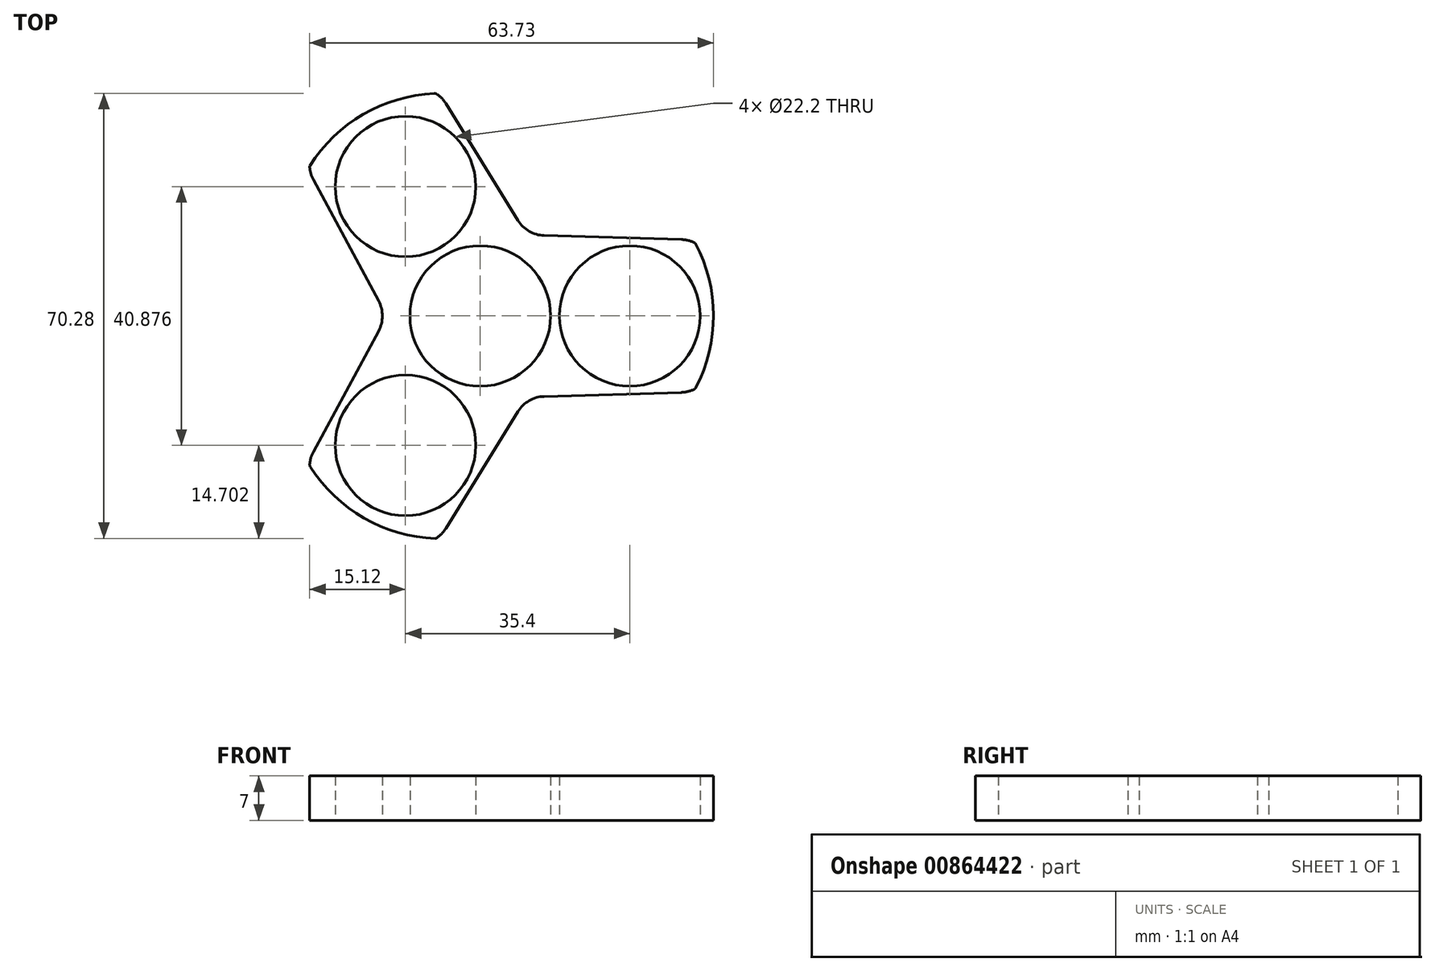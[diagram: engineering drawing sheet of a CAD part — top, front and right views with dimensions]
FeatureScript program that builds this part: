
annotation { "Feature Type Name" : "Feature", "Feature Type Description" : "" }
export const myFeature = defineFeature(function(context is Context, id is Id, definition is map)
    precondition{}
    {
        {
            var Q0;
            Q0=qCreatedBy(makeId("Top.planeOp"),FACE);
            var sketch = newSketch(context, id + "F0", { "sketchPlane" : qUnion([Q0])});
            skCircle(sketch, "E0", {"center": v(0, 0) * mm, "radius": 11.1 * mm});
            skPoint(sketch, "E1.startSnap0", {"position": v(14, 6.97) * mm});
            skPoint(sketch, "E1.start.orphan", {"position": v(14, 5.26) * mm});
            skPoint(sketch, "E2.orphan", {"position": v(17.77, 8.18) * mm});
            skPoint(sketch, "E3.start.orphan", {"position": v(10.05, 8.18) * mm});
            skPoint(sketch, "E4.end.orphan", {"position": v(10.05, -8.18) * mm});
            skPoint(sketch, "E4.start.orphan", {"position": v(17.77, -8.18) * mm});
            skPoint(sketch, "E5.trimOffspring.end.orphan", {"position": v(17.77, 0) * mm});
            skPoint(sketch, "E6.end.orphan", {"position": v(10.05, 0) * mm});
            skPoint(sketch, "E7.MirrorCS.end.orphan", {"position": v(-10.05, -8.18) * mm});
            skPoint(sketch, "E7.MirrorCS.start.orphan", {"position": v(-17.77, -8.18) * mm});
            skPoint(sketch, "E8.MirrorCS.end.orphan", {"position": v(-17.77, 8.18) * mm});
            skPoint(sketch, "E9.MirrorCS.start.orphan", {"position": v(-10.05, 8.18) * mm});
            skPoint(sketch, "E10.orphan", {"position": v(27.87, -13) * mm});
            skPoint(sketch, "E11.orphan", {"position": v(0, -13) * mm});
            skPoint(sketch, "E12.orphan", {"position": v(27.87, 13) * mm});
            skPoint(sketch, "E13.orphan", {"position": v(0, 13) * mm});
            skPoint(sketch, "E14.visualSharp", {"position": v(32.77, -12.04) * mm});
            skArc(sketch, "E14.filletArc", {"start": v(31.76, -12.07) * mm, "mid": v(32.77, -11.94) * mm, "end": v(33.74, -11.6) * mm});
            skPoint(sketch, "E15.visualSharp", {"position": v(32.77, 12.04) * mm});
            skArc(sketch, "E15.filletArc", {"start": v(33.88, 11.53) * mm, "mid": v(32.85, 11.92) * mm, "end": v(31.76, 12.07) * mm});
            skPoint(sketch, "E16.orphan", {"position": v(11.26, 6.5) * mm});
            skLineSegment(sketch, "E17.trimOffspring", {"start": v(10.07, 12.7) * mm, "end": v(31.76, 12.07) * mm});
            skPoint(sketch, "E18.orphan", {"position": v(11.26, -6.5) * mm});
            skLineSegment(sketch, "E19.trimOffspring", {"start": v(10.07, -12.7) * mm, "end": v(31.76, -12.07) * mm});
            skPoint(sketch, "E20.orphan", {"position": v(-11.26, -6.5) * mm});
            skPoint(sketch, "E21.visualSharp", {"position": v(7.38, -12.78) * mm});
            skPoint(sketch, "E22.visualSharp", {"position": v(7.38, 12.78) * mm});
            skArc(sketch, "E22.filletArc", {"start": v(5.97, 15.08) * mm, "mid": v(7.72, 13.37) * mm, "end": v(10.07, 12.7) * mm});
            skPoint(sketch, "E23.visualSharp", {"position": v(-14.76, 0) * mm});
            skPoint(sketch, "E24.end.orphan", {"position": v(32.77, 0) * mm});
            skCircle(sketch, "E25", {"center": v(23.6, 0) * mm, "radius": 11.1 * mm});
            skPoint(sketch, "E26.center.orphan", {"position": v(27.87, 0) * mm});
            skArc(sketch, "E27", {"start": v(34.05, -11.3) * mm, "mid": v(36.81, 0.07) * mm, "end": v(33.98, 11.43) * mm});
            skPoint(sketch, "E28.visualSharp", {"position": v(33.95, 11.5) * mm});
            skArc(sketch, "E28.filletArc", {"start": v(33.98, 11.43) * mm, "mid": v(33.94, 11.49) * mm, "end": v(33.88, 11.53) * mm});
            skPoint(sketch, "E29.visualSharp", {"position": v(33.95, -11.5) * mm});
            skArc(sketch, "E29.filletArc", {"start": v(33.74, -11.6) * mm, "mid": v(33.92, -11.47) * mm, "end": v(34.05, -11.3) * mm});
            skCircle(sketch, "E30.1.0", {"center": v(-11.8, 20.44) * mm, "radius": 11.1 * mm});
            skArc(sketch, "E30.1.1", {"start": v(-7.24, 35.14) * mm, "mid": v(-18.47, 31.84) * mm, "end": v(-26.89, 23.71) * mm});
            skLineSegment(sketch, "E30.1.2", {"start": v(-16.04, 2.37) * mm, "end": v(-26.33, 21.47) * mm});
            skArc(sketch, "E30.1.3", {"start": v(-16.04, -2.37) * mm, "mid": v(-15.44, 0) * mm, "end": v(-16.04, 2.37) * mm});
            skLineSegment(sketch, "E30.1.4", {"start": v(5.97, 15.08) * mm, "end": v(-5.42, 33.54) * mm});
            skCircle(sketch, "E30.2.0", {"center": v(-11.8, -20.44) * mm, "radius": 11.1 * mm});
            skArc(sketch, "E30.2.1", {"start": v(-26.8, -23.84) * mm, "mid": v(-18.34, -31.92) * mm, "end": v(-7.1, -35.14) * mm});
            skLineSegment(sketch, "E30.2.2", {"start": v(5.97, -15.08) * mm, "end": v(-5.42, -33.54) * mm});
            skArc(sketch, "E30.2.3", {"start": v(10.07, -12.7) * mm, "mid": v(7.72, -13.37) * mm, "end": v(5.97, -15.08) * mm});
            skLineSegment(sketch, "E30.2.4", {"start": v(-16.04, -2.37) * mm, "end": v(-26.33, -21.47) * mm});
            skArc(sketch, "E31.1.0", {"start": v(-26.92, 23.58) * mm, "mid": v(-26.74, 22.49) * mm, "end": v(-26.33, 21.47) * mm});
            skArc(sketch, "E31.1.1", {"start": v(-26.89, 23.71) * mm, "mid": v(-26.92, 23.65) * mm, "end": v(-26.92, 23.58) * mm});
            skArc(sketch, "E31.1.2", {"start": v(-6.83, 35.02) * mm, "mid": v(-7.02, 35.11) * mm, "end": v(-7.24, 35.14) * mm});
            skArc(sketch, "E31.1.3", {"start": v(-5.42, 33.54) * mm, "mid": v(-6.05, 34.35) * mm, "end": v(-6.83, 35.02) * mm});
            skArc(sketch, "E31.2.0", {"start": v(-6.96, -35.1) * mm, "mid": v(-6.1, -34.4) * mm, "end": v(-5.42, -33.54) * mm});
            skArc(sketch, "E31.2.1", {"start": v(-7.1, -35.14) * mm, "mid": v(-7.02, -35.13) * mm, "end": v(-6.96, -35.1) * mm});
            skArc(sketch, "E31.2.2", {"start": v(-26.91, -23.42) * mm, "mid": v(-26.9, -23.64) * mm, "end": v(-26.8, -23.84) * mm});
            skArc(sketch, "E31.2.3", {"start": v(-26.33, -21.47) * mm, "mid": v(-26.72, -22.41) * mm, "end": v(-26.91, -23.42) * mm});
            skSolve(sketch);
        }
        {
            var Q0;
            Q0 = qSketchRegion(id + "F0", true);
            extrude(context, id + "F1", {"entities" : qUnion([Q0]), "depth" : 7 * mm, "offsetDistance" : 25 * mm});
        }
    });
